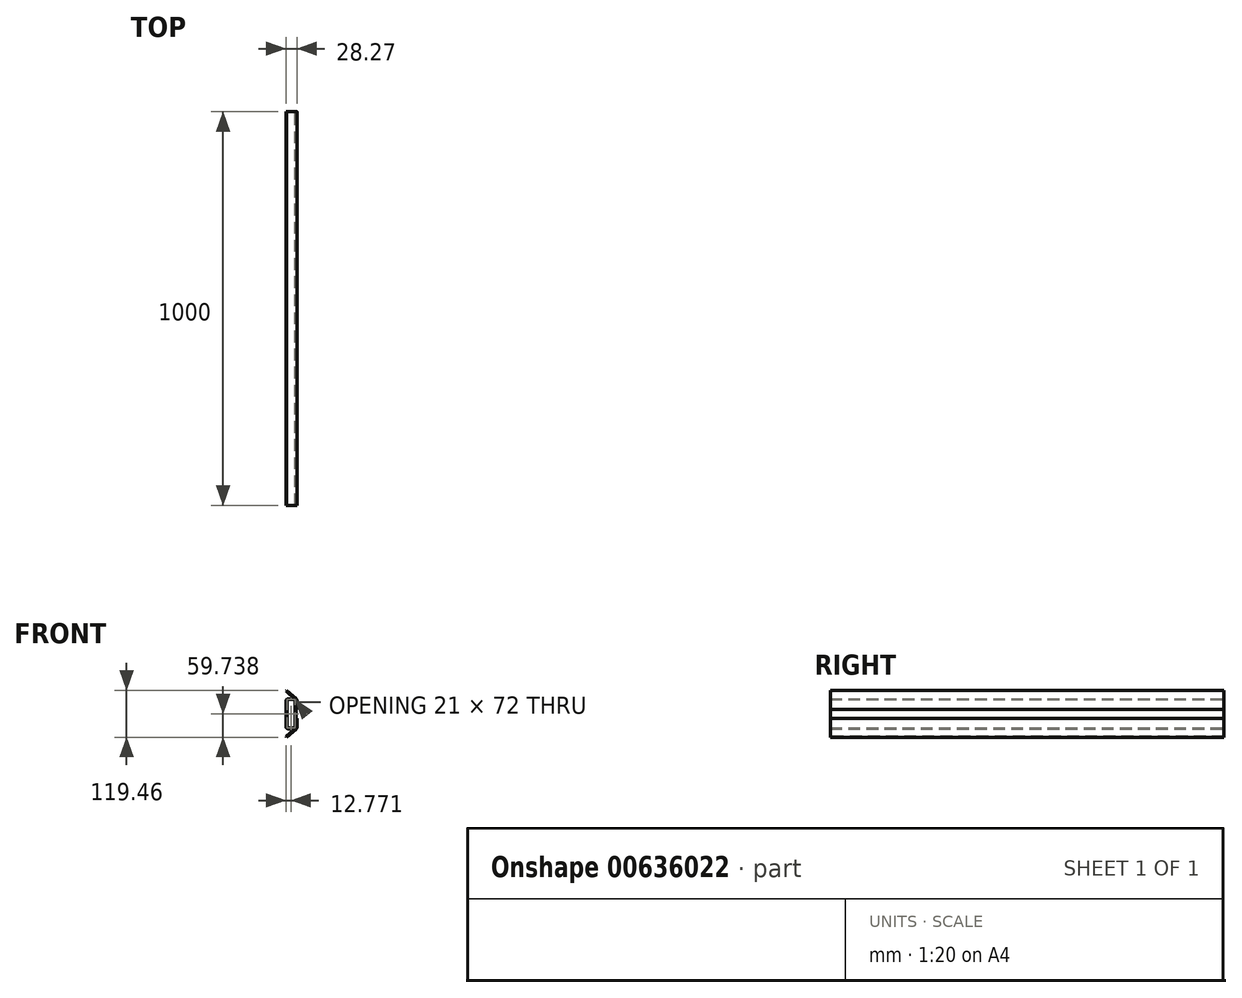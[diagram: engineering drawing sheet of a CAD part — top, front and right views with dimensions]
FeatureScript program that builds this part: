
annotation { "Feature Type Name" : "Feature", "Feature Type Description" : "" }
export const myFeature = defineFeature(function(context is Context, id is Id, definition is map)
    precondition{}
    {
        {
            var Q0;
            Q0=qCreatedBy(makeId("Front.planeOp"),FACE);
            var sketch = newSketch(context, id + "F0", { "sketchPlane" : qUnion([Q0])});
            skLineSegment(sketch, "E0", {"start": v(0, 25) * mm, "end": v(-26.29, 48.1) * mm});
            skLineSegment(sketch, "E1", {"start": v(-26.29, 48.1) * mm, "end": v(-28.27, 45.85) * mm});
            skLineSegment(sketch, "E2", {"start": v(-28.27, 45.85) * mm, "end": v(-3, 23.64) * mm});
            skLineSegment(sketch, "E3", {"start": v(0, 25) * mm, "end": v(0, 0) * mm});
            skLineSegment(sketch, "E4", {"start": v(0, 0) * mm, "end": v(-3, 0) * mm});
            skLineSegment(sketch, "E5", {"start": v(-3, 0) * mm, "end": v(-3, 23.64) * mm});
            skSolve(sketch);
        }
        {
            var Q0;
            Q0=makeQuery(id+"F0.imprint","IMPRINT",FACE,{"disambiguationData":[TD([[makeQuery(id+"F0.imprint","IMPRINT",EDGE,{"derivedFrom":sQuery(id+"F0.wireOp",EDGE,"E0")}),1.0]])]});
            extrude(context, id + "F1", {"entities" : qUnion([Q0]), "oppositeDirection" : true, "depth" : 1000 * mm, "offsetDistance" : 25 * mm, "symmetric" : true});
        }
        {
            var Q0;
            Q0=makeQuery(id+"F1.opExtrude","SWEPT_EDGE",EDGE,{"disambiguationData":[OSD([sQuery(id+"F0.wireOp",EDGE,"E0"),sQuery(id+"F0.wireOp",EDGE,"E3")])]});
            fillet(context, id + "F2", {"entities" : qUnion([Q0]), "radius" : 9 * mm, "tangentPropagation" : true, "allowEdgeOverflow" : false});
        }
        {
            var Q0;
            Q0=makeQuery(id+"F1.opExtrude","SWEPT_EDGE",EDGE,{"disambiguationData":[OSD([sQuery(id+"F0.wireOp",EDGE,"E2"),sQuery(id+"F0.wireOp",EDGE,"E5")])]});
            fillet(context, id + "F3", {"entities" : qUnion([Q0]), "radius" : 5 * mm, "tangentPropagation" : true, "allowEdgeOverflow" : false});
        }
        {
            var Q0;
            Q0=qCreatedBy(makeId("Front.planeOp"),FACE);
            var sketch = newSketch(context, id + "F4", { "sketchPlane" : qUnion([Q0])});
            skLineSegment(sketch, "E6.bottom", {"start": v(-12.85, -38.6) * mm, "end": v(-37.85, -38.6) * mm});
            skLineSegment(sketch, "E6.top", {"start": v(-12.85, -114.6) * mm, "end": v(-37.85, -114.6) * mm});
            skLineSegment(sketch, "E6.left", {"start": v(-12.85, -38.6) * mm, "end": v(-12.85, -114.6) * mm});
            skLineSegment(sketch, "E6.right", {"start": v(-37.85, -38.6) * mm, "end": v(-37.85, -114.6) * mm});
            skLineSegment(sketch, "E7.0", {"start": v(-14.85, -40.6) * mm, "end": v(-35.85, -40.6) * mm});
            skLineSegment(sketch, "E7.1", {"start": v(-14.85, -40.6) * mm, "end": v(-14.85, -112.6) * mm});
            skLineSegment(sketch, "E7.2", {"start": v(-14.85, -112.6) * mm, "end": v(-35.85, -112.6) * mm});
            skLineSegment(sketch, "E7.3", {"start": v(-35.85, -40.6) * mm, "end": v(-35.85, -112.6) * mm});
            skSolve(sketch);
        }
        {
            var Q0;
            Q0=makeQuery(id+"F4.imprint","IMPRINT",FACE,{"disambiguationData":[TD([[makeQuery(id+"F4.imprint","IMPRINT",EDGE,{"derivedFrom":sQuery(id+"F4.wireOp",EDGE,"E6.bottom")}),1.0]])]});
            extrude(context, id + "F5", {"entities" : qUnion([Q0]), "depth" : 1000 * mm, "offsetDistance" : 25 * mm, "symmetric" : true});
        }
        {
            var Q0;
            Q0=makeQuery(id+"F5.opExtrude","SWEPT_EDGE",EDGE,{"disambiguationData":[OSD([sQuery(id+"F4.wireOp",EDGE,"E7.0"),sQuery(id+"F4.wireOp",EDGE,"E7.3")])]});
            var Q1;
            Q1=makeQuery(id+"F5.opExtrude","SWEPT_EDGE",EDGE,{"disambiguationData":[OSD([sQuery(id+"F4.wireOp",EDGE,"E7.2"),sQuery(id+"F4.wireOp",EDGE,"E7.3")])]});
            var Q2;
            Q2=makeQuery(id+"F5.opExtrude","SWEPT_EDGE",EDGE,{"disambiguationData":[OSD([sQuery(id+"F4.wireOp",EDGE,"E7.0"),sQuery(id+"F4.wireOp",EDGE,"E7.1")])]});
            var Q3;
            Q3=makeQuery(id+"F5.opExtrude","SWEPT_EDGE",EDGE,{"disambiguationData":[OSD([sQuery(id+"F4.wireOp",EDGE,"E7.1"),sQuery(id+"F4.wireOp",EDGE,"E7.2")])]});
            fillet(context, id + "F6", {"entities" : qUnion([Q0, Q1, Q2, Q3]), "radius" : 3 * mm, "tangentPropagation" : true, "allowEdgeOverflow" : false});
        }
        {
            var Q0;
            Q0=makeQuery(id+"F5.opExtrude","SWEPT_EDGE",EDGE,{"disambiguationData":[OSD([sQuery(id+"F4.wireOp",EDGE,"E6.bottom"),sQuery(id+"F4.wireOp",EDGE,"E6.right")])]});
            var Q1;
            Q1=makeQuery(id+"F5.opExtrude","SWEPT_EDGE",EDGE,{"disambiguationData":[OSD([sQuery(id+"F4.wireOp",EDGE,"E6.bottom"),sQuery(id+"F4.wireOp",EDGE,"E6.left")])]});
            var Q2;
            Q2=makeQuery(id+"F5.opExtrude","SWEPT_EDGE",EDGE,{"disambiguationData":[OSD([sQuery(id+"F4.wireOp",EDGE,"E6.top"),sQuery(id+"F4.wireOp",EDGE,"E6.left")])]});
            var Q3;
            Q3=makeQuery(id+"F5.opExtrude","SWEPT_EDGE",EDGE,{"disambiguationData":[OSD([sQuery(id+"F4.wireOp",EDGE,"E6.top"),sQuery(id+"F4.wireOp",EDGE,"E6.right")])]});
            fillet(context, id + "F7", {"entities" : qUnion([Q0, Q1, Q2, Q3]), "radius" : 5 * mm, "tangentPropagation" : true, "allowEdgeOverflow" : false});
        }
        {
            var Q0;
            Q0=makeQuery(id+"F5.opExtrude","SWEPT_BODY",BODY,{"disambiguationData":[OSD([sQuery(id+"F4.wireOp",EDGE,"E6.bottom"),sQuery(id+"F4.wireOp",EDGE,"E6.top"),sQuery(id+"F4.wireOp",EDGE,"E6.left"),sQuery(id+"F4.wireOp",EDGE,"E6.right"),sQuery(id+"F4.wireOp",EDGE,"E7.0"),sQuery(id+"F4.wireOp",EDGE,"E7.1"),sQuery(id+"F4.wireOp",EDGE,"E7.2"),sQuery(id+"F4.wireOp",EDGE,"E7.3")])]});
            transform(context, id + "F8", {"entities" : qUnion([Q0]), "transformType" : TransformType.TRANSLATION_3D, "dx" : 9.85 * mm, "dy" : 0 * mm, "dz" : 67.65 * mm, "makeCopy" : false});
        }
        {
            var Q0;
            Q0=makeQuery(id+"F1.opExtrude","SWEPT_BODY",BODY,{"disambiguationData":[OSD([sQuery(id+"F0.wireOp",EDGE,"E0"),sQuery(id+"F0.wireOp",EDGE,"E1"),sQuery(id+"F0.wireOp",EDGE,"E2"),sQuery(id+"F0.wireOp",EDGE,"E3"),sQuery(id+"F0.wireOp",EDGE,"E4"),sQuery(id+"F0.wireOp",EDGE,"E5")])]});
            var Q1;
            Q1=qCreatedBy(makeId("Top.planeOp"),FACE);
            mirror(context, id + "F9", {"entities" : qUnion([Q0]), "mirrorPlane" : qUnion([Q1])});
        }
        {
            var Q0;
            Q0=makeQuery(id+"F9.opPattern","COPY",BODY,{"derivedFrom":makeQuery(id+"F1.opExtrude","SWEPT_BODY",BODY,{"disambiguationData":[OSD([sQuery(id+"F0.wireOp",EDGE,"E0"),sQuery(id+"F0.wireOp",EDGE,"E1"),sQuery(id+"F0.wireOp",EDGE,"E2"),sQuery(id+"F0.wireOp",EDGE,"E3"),sQuery(id+"F0.wireOp",EDGE,"E4"),sQuery(id+"F0.wireOp",EDGE,"E5")])]}),"instanceName":"1"});
            transform(context, id + "F10", {"entities" : qUnion([Q0]), "transformType" : TransformType.TRANSLATION_3D, "dx" : 0 * mm, "dy" : 0 * mm, "dz" : -17.82 * mm, "makeCopy" : false});
        }
        {
            var Q0;
            Q0=makeQuery(id+"F1.opExtrude","SWEPT_BODY",BODY,{"disambiguationData":[OSD([sQuery(id+"F0.wireOp",EDGE,"E0"),sQuery(id+"F0.wireOp",EDGE,"E1"),sQuery(id+"F0.wireOp",EDGE,"E2"),sQuery(id+"F0.wireOp",EDGE,"E3"),sQuery(id+"F0.wireOp",EDGE,"E4"),sQuery(id+"F0.wireOp",EDGE,"E5")])]});
            transform(context, id + "F11", {"entities" : qUnion([Q0]), "transformType" : TransformType.TRANSLATION_3D, "dx" : 0 * mm, "dy" : 0 * mm, "dz" : 2.67 * mm, "makeCopy" : false});
        }
        {
            var Q0;
            Q0=makeQuery(id+"F9.opPattern","COPY",BODY,{"derivedFrom":makeQuery(id+"F1.opExtrude","SWEPT_BODY",BODY,{"disambiguationData":[OSD([sQuery(id+"F0.wireOp",EDGE,"E0"),sQuery(id+"F0.wireOp",EDGE,"E1"),sQuery(id+"F0.wireOp",EDGE,"E2"),sQuery(id+"F0.wireOp",EDGE,"E3"),sQuery(id+"F0.wireOp",EDGE,"E4"),sQuery(id+"F0.wireOp",EDGE,"E5")])]}),"instanceName":"1"});
            transform(context, id + "F12", {"entities" : qUnion([Q0]), "transformType" : TransformType.TRANSLATION_3D, "dx" : 0 * mm, "dy" : 0 * mm, "dz" : -2.75 * mm, "makeCopy" : false});
        }
    });
